# Revit family: VLGFP1502-xxxWS8xxBxxxx
name_source: partatom
category: Oprawy oświetleniowe
revit_build: Autodesk Revit 2017 (Build: 20190508_0315(x64)
units: mm (PartAtom-declared; Revit-internal decimal feet)

## family parameters
Numer OmniClass = 23.80.70.11
Obiekt nadrzędny = Powierzchnia
Punkt obliczania pomieszczeń = Nie
Tnij formami wycięć po wczytaniu = Nie
Typ części = Normalny
Tytuł OmniClass = Luminaries for Internal Lighting
Współdzielony = Nie
Wymiar okrągłego złącza = Użyj średnicy
Źródło światła = Tak

## types (19) — shared parameters
Emituj kształt widoczny w renderingu = Nie
Emituj z długości prostokąta = 63 mm  [stored 0.206693 ft]
Emituj z szerokości prostokąta = 1469 mm  [stored 4.81955 ft]
Filtr koloru = 16777215
Kod zespołu = D5020200
Lampa = LED
Odchylenie kierunku = 90.00°
Plik sieci fotometrycznej = VLGFP1501-5NDWS840B0800.IES
Producent = RIDI Leuchten GmbH
URL = www.ridi.de
Zmiana temperatury barwowej przyciemniania lampy = <Brak>
brand = RIDI
conformity mark = CE
electrical safety class = 1
ingress protection (IP) code = IP54
length = 1500 mm  [stored 4.92126 ft]
nominal frequency = 50-60Hz
nominal voltage = 230
voltage type (AC, DC, UC) = AC
weight = 1.9 kg
zero-valued in all types: Domyślna rzędna

## per-type parameters (varying)
| type | Model | Obciążenie pozorne | height | rated input power | width |
| VLGFP1502-5NDWS830B1400 | 1551036 | 100 VA | 66 mm  [stored 0.216535 ft] | 100 | 67 mm |
| VLGFP1502-7DAWS830B1400 | 1561036 | 100 VA | 66 mm  [stored 0.216535 ft] | 100 | 67 mm |
| VLGFP1502-7DAWS830B1700 | 1561094 | 121 VA | 66 mm  [stored 0.216535 ft] | 121 | 67 mm |
| VLGFP1502-5NDWS830B1500-RF | 1551108 | 100 VA | 66 mm  [stored 0.216535 ft] | 100 | 67 mm |
| VLGFP1502-5NDWS840B1500 | 1551017 | 100 VA | 66 mm  [stored 0.216535 ft] | 100 | 67 mm |
| VLGFP1502-7DAWS840B1500 | 1561017
1561017 | 100 VA | 66 mm  [stored 0.216535 ft] | 100 | 67 mm |
| VLGFP1502-7DASI840B1700 | 1561091 | 121 VA | 66 mm  [stored 0.216535 ft] | 121 | 67 mm |
| VLGFP1502-5NDWS840B1500-RF | 1551104 | 100 VA | 66 mm  [stored 0.216535 ft] | 100 | 67 mm |
| VLGFP1502-5NDWS850B1500 | 1551049 | 100 VA | 66 mm  [stored 0.216535 ft] | 100 | 67 mm |
| VLGFP1502-7DAWS850B1500 | 1561049 | 100 VA | 81 mm  [stored 0.265748 ft] | 100 | 66 mm  [stored 0.216535 ft] |
| VLGFP1502-5NDWS850B1800 | 1551097 | 121 VA | 66 mm  [stored 0.216535 ft] | 121 | 67 mm |
| VLGFP1502-7DAWS850B1800 | 1561097 | 121 VA | 81 mm  [stored 0.265748 ft] | 121 | 66 mm  [stored 0.216535 ft] |
| VLGFP1502-5NDWS850B1600-RF | 1551110 | 100 VA | 66 mm  [stored 0.216535 ft] | 100 | 67 mm |
| VLGFP1502-5NDWS865B1500 | 1551062 | 100 VA | 66 mm  [stored 0.216535 ft] | 100 | 67 mm |
| VLGFP1502-5NDWS830B1700 | 1551094 | 121 VA | 81 mm  [stored 0.265748 ft] | 121 | 66 mm  [stored 0.216535 ft] |
| VLGFP1502-5NDWS865B1700 | 1551101 | 121 VA | 66 mm  [stored 0.216535 ft] | 121 | 67 mm |
| VLGFP1502-7DAWS865B1700 | 1561101 | 121 VA | 66 mm  [stored 0.216535 ft] | 121 | 67 mm |
| VLGFP1502-5NDWS865B1500-RF | 1551106 | 100 VA | 66 mm  [stored 0.216535 ft] | 100 | 67 mm |
| VLGFP1502-5NDSI840B1700 | 1551091 | 121 VA | 81 mm  [stored 0.265748 ft] | 121 | 66 mm  [stored 0.216535 ft] |

note: column(s) folded — value = type name in every type: product name

note: [stored X ft] marks values corroborated as IEEE doubles in the binary element streams (Revit-internal decimal feet)
